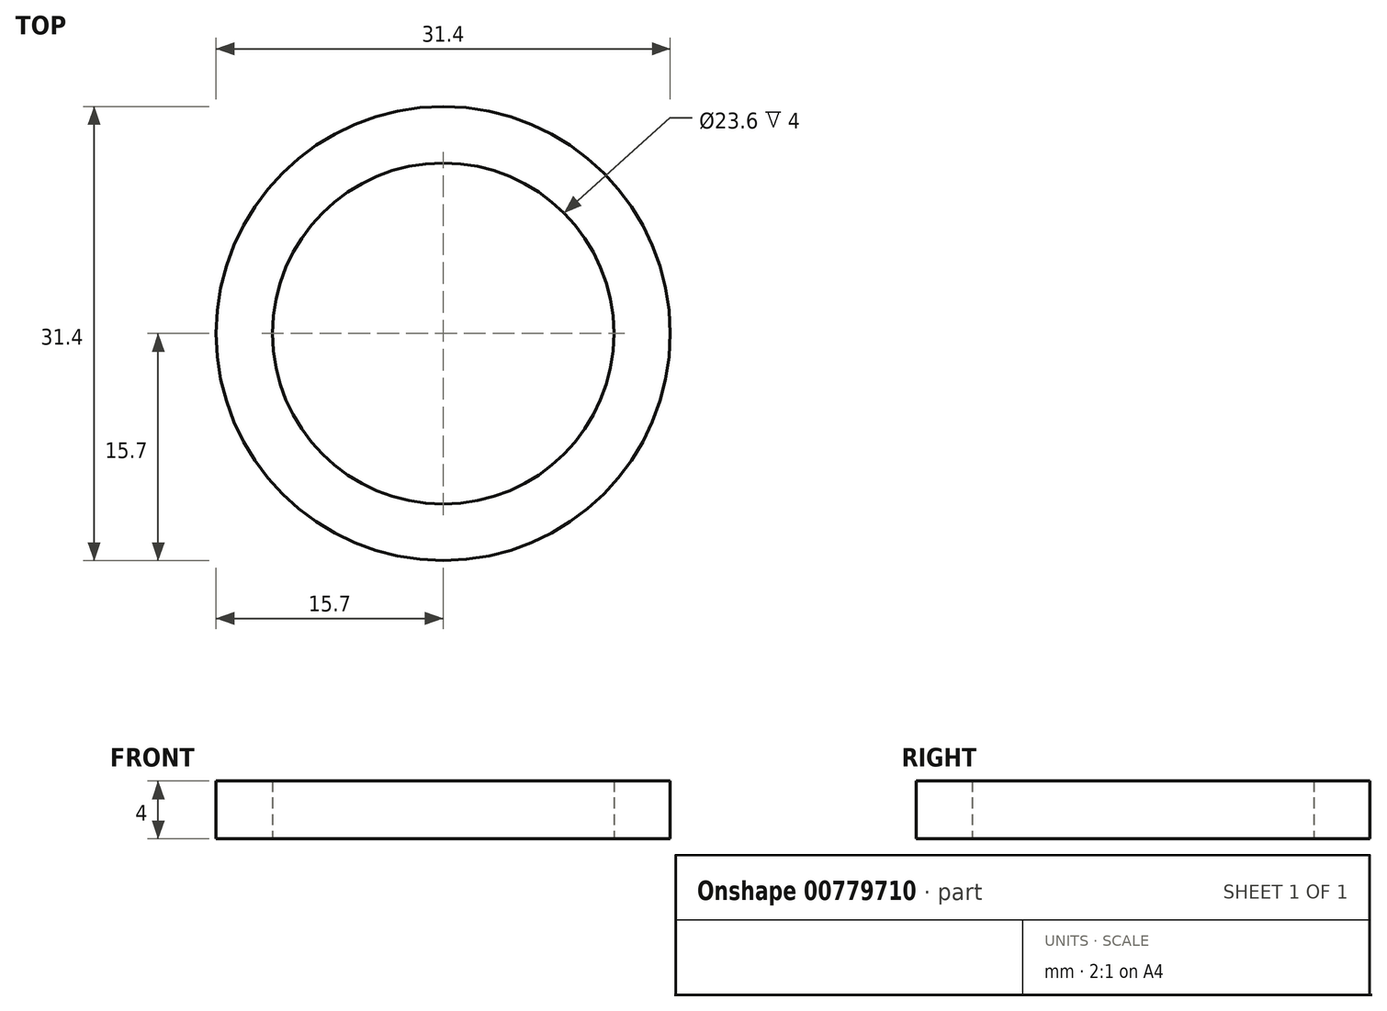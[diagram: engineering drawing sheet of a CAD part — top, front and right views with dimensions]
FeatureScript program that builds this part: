
annotation { "Feature Type Name" : "Feature", "Feature Type Description" : "" }
export const myFeature = defineFeature(function(context is Context, id is Id, definition is map)
    precondition{}
    {
        {
            var Q0;
            Q0=qCreatedBy(makeId("Top.planeOp"),FACE);
            var sketch = newSketch(context, id + "F0", { "sketchPlane" : qUnion([Q0])});
            skCircle(sketch, "E0", {"center": v(0, 0) * mm, "radius": 11.8 * mm});
            skSolve(sketch);
        }
        {
            var Q0;
            Q0 = qSketchRegion(id + "F0", true);
            extrude(context, id + "F1", {"entities" : qUnion([Q0]), "depth" : 4 * mm, "offsetDistance" : 25 * mm});
        }
        {
            var Q0;
            Q0=makeQuery(id+"F1.opExtrude","CAP_FACE",FACE,{"disambiguationData":[OSD([sQuery(id+"F0.wireOp",EDGE,"E0")])],"isStart":false});
            var Q1;
            Q1=makeQuery(id+"F1.opExtrude","CAP_FACE",FACE,{"disambiguationData":[OSD([sQuery(id+"F0.wireOp",EDGE,"E0")])],"isStart":true});
            shell(context, id + "F2", {"entities" : qUnion([Q0, Q1]), "thickness" : 3.9 * mm, "oppositeDirection" : true});
        }
    });
